# Revit family: product code 61920-S
name_source: partatom
category: Systemy meblowe
units: mm (PartAtom-declared; Revit-internal decimal feet)

## family parameters
Oparty na płaszczyźnie roboczej = Nie
Punkt obliczania pomieszczeń = Nie
Tnij formami wycięć po wczytaniu = Nie
Typ części = Normalny
Współdzielony = Nie
Wymiar okrągłego złącza = Użyj średnicy
Zawsze pionowo = Tak

## types (1)
- 61920-S-L
    Domyślna rzędna = 0 cm
    Height = 110 cm
    Hosted on larslaj.com = https://larslaj.com
    Kobenhagen Materials = larslaj.com/bim
    Lenght = 180 cm
    Maintenance = We recommend to examine and tighten all screws and bolt clamps after a few weeks’ use. In order to prevent cracks and to extend the life of the wood, it is recommended that the wood details should be oiled every 3-5 years.
    Material = Larch, stainless steel, powder coated steel
    Model = 61920-S-L
    Opis = Amager Bar Set
    Producent = Lars Laj
    Product Groups = Sets
    Product line = Amager
Amager
    Sit height = 75 cm
    Steel = Kobenhagen RAL 1013
    URL = https://kobenhagen.com
    Weight = 50 kg
    Width = 150 cm
    Wood = Kobenhagen Wood - Larch
